# Revit family: Котел_ТЕРМОТЕХНИК_ТТ50_ 210-2000 кВт
name_source: partatom
category: Оборудование
units: mm (PartAtom-declared; Revit-internal decimal feet)

## family parameters
Всегда вертикально = Да
Классификация = Нет
На основе рабочей плоскости = Нет
Общий = Нет
При загрузке вырезать с полостями = Нет
Размер круглого соединителя = Использовать диаметр
Тип детали = Нормальный
Точка расчета площади = Нет

## types (10) — shared parameters
G = 25 мм
URL = https://www.entroros.ru
Видимость_ВКЛ = Да
Видимость_ВЫКЛ = Нет
Изготовитель = ЭНТРОРОС
КПД (%) не менее = 94
Ключевая пометка = https://www.entroros.ru
Код по классификатору = D3020100
Материал_Условный BOX = <По категории>
Описание = Котел ЭНТРОРОС ТЕРМОТЕХНИК ТТ50
Производитель = ЭНТРОРОС
Семейство заказано = ООО ЭНТРОРОС (entroros.ru)
Семейство оборудования = ТТ50
Семейство разработано = ООО DASBIM (dasbim.ru)
Ссылка на документацию = https://www.entroros.ru
Штуцер_Датчик дым.газов_D = G1/2-B
Штуцер_Датчик темп. воды на входе_D = G1/2-B
Штуцер_Датчик темп. воды на выходе_D = G1/2-B
Штуцер_Слив воды_D = 40 мм
Штуцер_Слив воды_D_Формула = G1/2-B
Штуцер_Слив конденсата_D = 25 мм
Штуцер_Слив конденсата_D_Формула = G1-B
Штуцер_Тягонапоромер_D = G1/2-B
zero-valued in all types: Стоимость, Штуцер_Слив воды_А, Штуцер_Слив конденсата_А

## per-type parameters (varying)
- 01_250_ef_231Е: B=1040 мм; H=1313 мм; L=2526 мм; А_Дверь_Смещение наружной грани=2389 мм; Аэродин. сопротивление (Па)=500; Дверь_231е=Да; Дверь_234е=Нет; Дверь_235е=Нет; Дверь_237е=Нет; Дверь_239е=Нет; Комментарии к типоразмеру=210-250 кВт; Корпус_231е=Да; Корпус_234е=Нет; Корпус_235е=Нет; Корпус_237е=Нет; Корпус_239е=Нет; Масса (кг)=1087; Ном. мощность (кВт)=210-250 кВт; Подключение горелки=320; С_Ось котла=665 мм; Штуцер_Вход воды_D=100 мм; Штуцер_Вход воды_А=500 мм; Штуцер_Выход воды_D=100 мм; Штуцер_Выход воды_А=631 мм; Штуцер_Выход дыма_D=200 мм; Штуцер_Выход дыма_В=885 мм; Штуцер_Подключение горелки=320 мм; Штуцер_Пред.клапан_D=40 мм; Штуцер_Пред.клапан_А=400 мм; Штуцер_Слив воды_В=81 мм; Штуцер_Слив конденсата_В=266 мм
- 02_400_ef_232Е: B=1040 мм; H=1313 мм; L=2526 мм; А_Дверь_Смещение наружной грани=2389 мм; Аэродин. сопротивление (Па)=305; Дверь_231е=Да; Дверь_234е=Нет; Дверь_235е=Нет; Дверь_237е=Нет; Дверь_239е=Нет; Комментарии к типоразмеру=310-400 кВт; Корпус_231е=Да; Корпус_234е=Нет; Корпус_235е=Нет; Корпус_237е=Нет; Корпус_239е=Нет; Масса (кг)=1133; Ном. мощность (кВт)=310-400 кВт; Подключение горелки=320; С_Ось котла=665 мм; Штуцер_Вход воды_D=100 мм; Штуцер_Вход воды_А=500 мм; Штуцер_Выход воды_D=100 мм; Штуцер_Выход воды_А=631 мм; Штуцер_Выход дыма_D=200 мм; Штуцер_Выход дыма_В=885 мм; Штуцер_Подключение горелки=320 мм; Штуцер_Пред.клапан_D=40 мм; Штуцер_Пред.клапан_А=400 мм; Штуцер_Слив воды_В=81 мм; Штуцер_Слив конденсата_В=266 мм
- 03_560_ef_233Е: B=1210 мм; H=1483 мм; L=2648 мм; А_Дверь_Смещение наружной грани=2511 мм; Аэродин. сопротивление (Па)=200; Дверь_231е=Нет; Дверь_234е=Да; Дверь_235е=Нет; Дверь_237е=Нет; Дверь_239е=Нет; Комментарии к типоразмеру=420-560 кВт; Корпус_231е=Нет; Корпус_234е=Да; Корпус_235е=Нет; Корпус_237е=Нет; Корпус_239е=Нет; Масса (кг)=1508; Ном. мощность (кВт)=420-560 кВт; Подключение горелки=330; С_Ось котла=740 мм; Штуцер_Вход воды_D=100 мм; Штуцер_Вход воды_А=500 мм; Штуцер_Выход воды_D=100 мм; Штуцер_Выход воды_А=748 мм; Штуцер_Выход дыма_D=250 мм; Штуцер_Выход дыма_В=1030 мм; Штуцер_Подключение горелки=330 мм; Штуцер_Пред.клапан_D=50 мм; Штуцер_Пред.клапан_А=500 мм; Штуцер_Слив воды_В=81 мм; Штуцер_Слив конденсата_В=266 мм
- 04_660_ef_234Е: B=1210 мм; H=1483 мм; L=2648 мм; А_Дверь_Смещение наружной грани=2511 мм; Аэродин. сопротивление (Па)=365; Дверь_231е=Нет; Дверь_234е=Да; Дверь_235е=Нет; Дверь_237е=Нет; Дверь_239е=Нет; Комментарии к типоразмеру=561-660 кВт; Корпус_231е=Нет; Корпус_234е=Да; Корпус_235е=Нет; Корпус_237е=Нет; Корпус_239е=Нет; Масса (кг)=1571; Ном. мощность (кВт)=561-660 кВт; Подключение горелки=330; С_Ось котла=740 мм; Штуцер_Вход воды_D=100 мм; Штуцер_Вход воды_А=500 мм; Штуцер_Выход воды_D=100 мм; Штуцер_Выход воды_А=748 мм; Штуцер_Выход дыма_D=250 мм; Штуцер_Выход дыма_В=1030 мм; Штуцер_Подключение горелки=330 мм; Штуцер_Пред.клапан_D=50 мм; Штуцер_Пред.клапан_А=500 мм; Штуцер_Слив воды_В=81 мм; Штуцер_Слив конденсата_В=266 мм
- 05_870_ef_235Е: B=1330 мм; H=1603 мм; L=2869 мм; А_Дверь_Смещение наружной грани=2731 мм; Аэродин. сопротивление (Па)=260; Дверь_231е=Нет; Дверь_234е=Нет; Дверь_235е=Да; Дверь_237е=Нет; Дверь_239е=Нет; Комментарии к типоразмеру=661-870 кВт; Корпус_231е=Нет; Корпус_234е=Нет; Корпус_235е=Да; Корпус_237е=Нет; Корпус_239е=Нет; Масса (кг)=1940; Ном. мощность (кВт)=661-870 кВт; Подключение горелки=420; С_Ось котла=800 мм; Штуцер_Вход воды_D=125 мм; Штуцер_Вход воды_А=550 мм; Штуцер_Выход воды_D=125 мм; Штуцер_Выход воды_А=768 мм; Штуцер_Выход дыма_D=300 мм; Штуцер_Выход дыма_В=1150 мм; Штуцер_Подключение горелки=420 мм; Штуцер_Пред.клапан_D=50 мм; Штуцер_Пред.клапан_А=550 мм; Штуцер_Слив воды_В=81 мм; Штуцер_Слив конденсата_В=266 мм
- 06_1000_ef_236Е: B=1330 мм; H=1603 мм; L=2869 мм; А_Дверь_Смещение наружной грани=2731 мм; Аэродин. сопротивление (Па)=460; Дверь_231е=Нет; Дверь_234е=Нет; Дверь_235е=Да; Дверь_237е=Нет; Дверь_239е=Нет; Комментарии к типоразмеру=871-1000 кВт; Корпус_231е=Нет; Корпус_234е=Нет; Корпус_235е=Да; Корпус_237е=Нет; Корпус_239е=Нет; Масса (кг)=2021; Ном. мощность (кВт)=871-1000 кВт; Подключение горелки=420; С_Ось котла=800 мм; Штуцер_Вход воды_D=125 мм; Штуцер_Вход воды_А=550 мм; Штуцер_Выход воды_D=125 мм; Штуцер_Выход воды_А=768 мм; Штуцер_Выход дыма_D=300 мм; Штуцер_Выход дыма_В=1150 мм; Штуцер_Подключение горелки=420 мм; Штуцер_Пред.клапан_D=50 мм; Штуцер_Пред.клапан_А=550 мм; Штуцер_Слив воды_В=81 мм; Штуцер_Слив конденсата_В=266 мм
- 07_1360_ef_237Е: B=1490 мм; H=1751 мм; L=3283 мм; А_Дверь_Смещение наружной грани=3137 мм; Аэродин. сопротивление (Па)=425; Дверь_231е=Нет; Дверь_234е=Нет; Дверь_235е=Нет; Дверь_237е=Да; Дверь_239е=Нет; Комментарии к типоразмеру=1100-1360 кВт; Корпус_231е=Нет; Корпус_234е=Нет; Корпус_235е=Нет; Корпус_237е=Да; Корпус_239е=Нет; Масса (кг)=2777; Ном. мощность (кВт)=1100-1360 кВт; Подключение горелки=420; С_Ось котла=870 мм; Штуцер_Вход воды_D=125 мм; Штуцер_Вход воды_А=700 мм; Штуцер_Выход воды_D=125 мм; Штуцер_Выход воды_А=762 мм; Штуцер_Выход дыма_D=350 мм; Штуцер_Выход дыма_В=1290 мм; Штуцер_Подключение горелки=420 мм; Штуцер_Пред.клапан_D=65 мм; Штуцер_Пред.клапан_А=700 мм; Штуцер_Слив воды_В=71 мм; Штуцер_Слив конденсата_В=258 мм
- 08_1530_ef_238Е: B=1490 мм; H=1751 мм; L=3283 мм; А_Дверь_Смещение наружной грани=3137 мм; Аэродин. сопротивление (Па)=670; Дверь_231е=Нет; Дверь_234е=Нет; Дверь_235е=Нет; Дверь_237е=Да; Дверь_239е=Нет; Комментарии к типоразмеру=1361-1530 кВт; Корпус_231е=Нет; Корпус_234е=Нет; Корпус_235е=Нет; Корпус_237е=Да; Корпус_239е=Нет; Масса (кг)=2893; Ном. мощность (кВт)=1361-1530 кВт; Подключение горелки=420; С_Ось котла=870 мм; Штуцер_Вход воды_D=125 мм; Штуцер_Вход воды_А=700 мм; Штуцер_Выход воды_D=125 мм; Штуцер_Выход воды_А=762 мм; Штуцер_Выход дыма_D=350 мм; Штуцер_Выход дыма_В=1290 мм; Штуцер_Подключение горелки=420 мм; Штуцер_Пред.клапан_D=65 мм; Штуцер_Пред.клапан_А=700 мм; Штуцер_Слив воды_В=71 мм; Штуцер_Слив конденсата_В=258 мм
- 09_1740_ef_239Е: B=1640 мм; H=1901 мм; L=3491 мм; А_Дверь_Смещение наружной грани=3345 мм; Аэродин. сопротивление (Па)=500; Дверь_231е=Нет; Дверь_234е=Нет; Дверь_235е=Нет; Дверь_237е=Нет; Дверь_239е=Да; Комментарии к типоразмеру=1531-1740 кВт; Корпус_231е=Нет; Корпус_234е=Нет; Корпус_235е=Нет; Корпус_237е=Нет; Корпус_239е=Да; Масса (кг)=3509; Ном. мощность (кВт)=1531-1740 кВт; Подключение горелки=420; С_Ось котла=945 мм; Штуцер_Вход воды_D=150 мм; Штуцер_Вход воды_А=700 мм; Штуцер_Выход воды_D=150 мм; Штуцер_Выход воды_А=920 мм; Штуцер_Выход дыма_D=350 мм; Штуцер_Выход дыма_В=1435 мм; Штуцер_Подключение горелки=420 мм; Штуцер_Пред.клапан_D=80 мм; Штуцер_Пред.клапан_А=700 мм; Штуцер_Слив воды_В=71 мм; Штуцер_Слив конденсата_В=258 мм
- 10_2000_ef_240Е: B=1640 мм; H=1901 мм; L=3491 мм; А_Дверь_Смещение наружной грани=3345 мм; Аэродин. сопротивление (Па)=648; Дверь_231е=Нет; Дверь_234е=Нет; Дверь_235е=Нет; Дверь_237е=Нет; Дверь_239е=Да; Комментарии к типоразмеру=1741-2000 кВт; Корпус_231е=Нет; Корпус_234е=Нет; Корпус_235е=Нет; Корпус_237е=Нет; Корпус_239е=Да; Масса (кг)=3656; Ном. мощность (кВт)=1741-2000 кВт; Подключение горелки=420; С_Ось котла=945 мм; Штуцер_Вход воды_D=150 мм; Штуцер_Вход воды_А=700 мм; Штуцер_Выход воды_D=150 мм; Штуцер_Выход воды_А=920 мм; Штуцер_Выход дыма_D=350 мм; Штуцер_Выход дыма_В=1435 мм; Штуцер_Подключение горелки=420 мм; Штуцер_Пред.клапан_D=80 мм; Штуцер_Пред.клапан_А=700 мм; Штуцер_Слив воды_В=71 мм; Штуцер_Слив конденсата_В=258 мм
